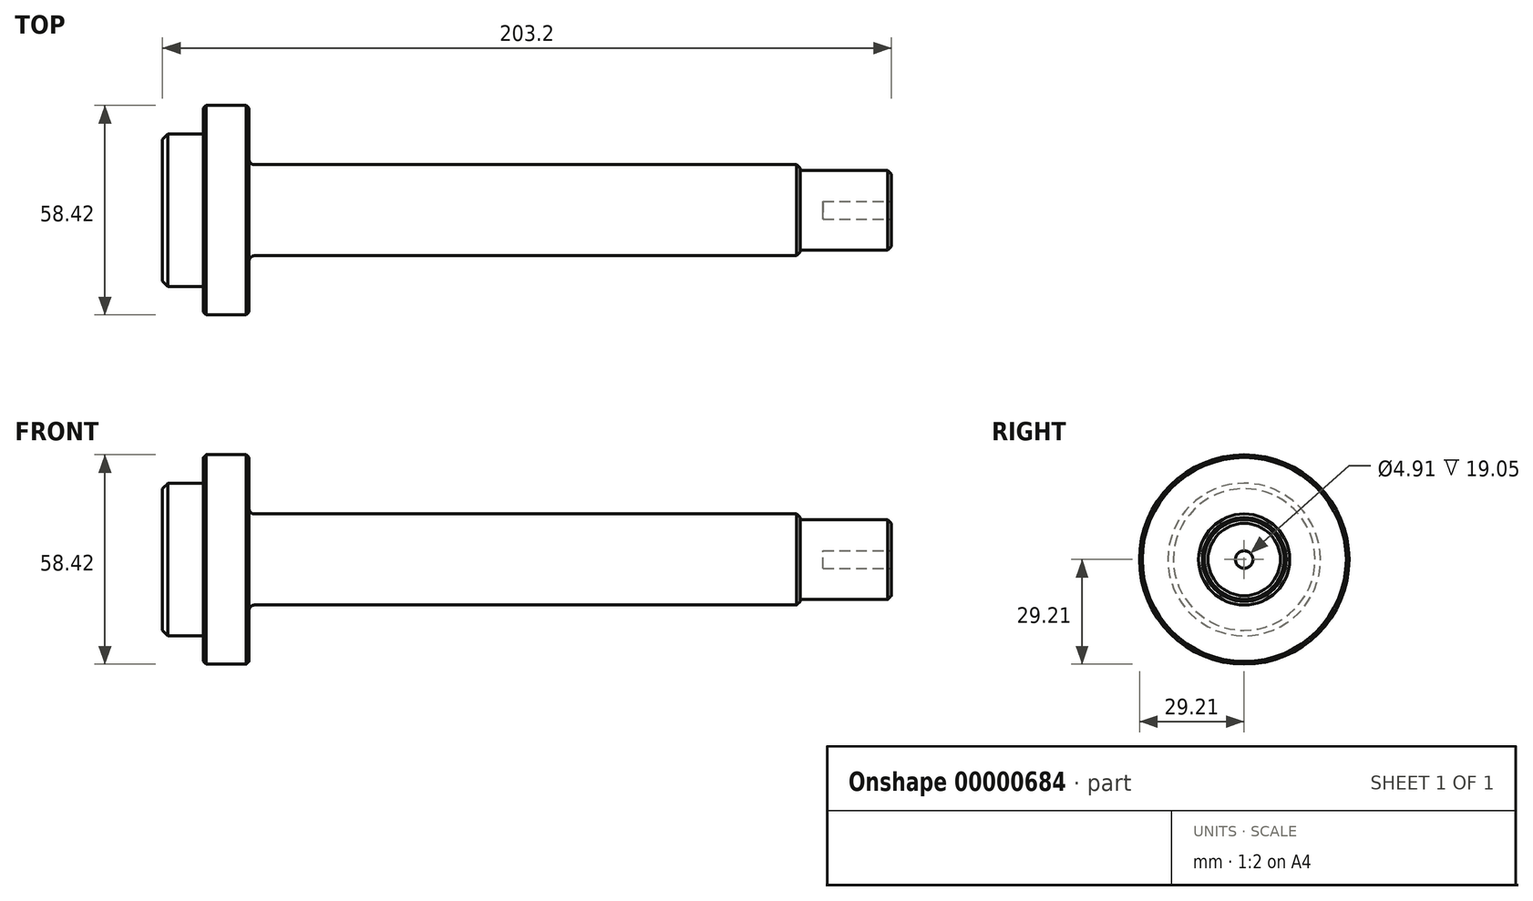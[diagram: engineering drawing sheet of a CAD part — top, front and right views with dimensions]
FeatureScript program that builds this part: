
annotation { "Feature Type Name" : "Feature", "Feature Type Description" : "" }
export const myFeature = defineFeature(function(context is Context, id is Id, definition is map)
    precondition{}
    {
        {
            var Q0;
            Q0=qCreatedBy(makeId("Front.planeOp"),FACE);
            var sketch = newSketch(context, id + "F0", { "sketchPlane" : qUnion([Q0])});
            skLineSegment(sketch, "E0", {"start": v(0, 0) * mm, "end": v(203.2, 0) * mm, "construction": true});
            skLineSegment(sketch, "E1", {"start": v(0, 0) * mm, "end": v(0, 21.27) * mm});
            skLineSegment(sketch, "E2", {"start": v(0, 21.27) * mm, "end": v(11.43, 21.27) * mm});
            skLineSegment(sketch, "E3", {"start": v(11.43, 21.27) * mm, "end": v(11.43, 29.2) * mm});
            skLineSegment(sketch, "E4", {"start": v(11.43, 29.2) * mm, "end": v(24.13, 29.2) * mm});
            skLineSegment(sketch, "E5", {"start": v(24.13, 29.2) * mm, "end": v(24.13, 14.22) * mm});
            skLineSegment(sketch, "E6", {"start": v(25.65, 12.7) * mm, "end": v(177.8, 12.7) * mm});
            skLineSegment(sketch, "E7", {"start": v(177.8, 12.7) * mm, "end": v(177.8, 11.11) * mm});
            skLineSegment(sketch, "E8", {"start": v(177.8, 11.11) * mm, "end": v(203.2, 11.11) * mm});
            skLineSegment(sketch, "E9", {"start": v(203.2, 11.11) * mm, "end": v(203.2, 0) * mm});
            skLineSegment(sketch, "E10", {"start": v(0, 0) * mm, "end": v(203.2, 0) * mm});
            skPoint(sketch, "E11.visualSharp", {"position": v(24.13, 12.7) * mm});
            skArc(sketch, "E11.filletArc", {"start": v(24.13, 14.22) * mm, "mid": v(24.58, 13.15) * mm, "end": v(25.65, 12.7) * mm});
            skSolve(sketch);
        }
        {
            var Q0;
            Q0=makeQuery(id+"F0.imprint","IMPRINT",FACE,{"disambiguationData":[TD([[makeQuery(id+"F0.imprint","IMPRINT",EDGE,{"derivedFrom":sQuery(id+"F0.wireOp",EDGE,"E1")}),-1.0]])]});
            var Q1;
            Q1=sQuery(id+"F0.wireOp",EDGE,"E10");
            revolve(context, id + "F1", {"entities" : qUnion([Q0]), "axis" : qUnion([Q1]), "revolveType" : RevolveType.FULL});
        }
        {
            var Q0;
            Q0=makeQuery(id+"F1.opRevolve","SWEPT_EDGE",EDGE,{"disambiguationData":[OSD([sQuery(id+"F0.wireOp",EDGE,"E3"),sQuery(id+"F0.wireOp",EDGE,"E4")])]});
            var Q1;
            Q1=makeQuery(id+"F1.opRevolve","SWEPT_EDGE",EDGE,{"disambiguationData":[OSD([sQuery(id+"F0.wireOp",EDGE,"E4"),sQuery(id+"F0.wireOp",EDGE,"E5")])]});
            chamfer(context, id + "F2", {"entities" : qUnion([Q0, Q1]), "chamferType" : ChamferType.OFFSET_ANGLE, "width" : 0.76 * mm, "oppositeDirection" : false, "angle" : 45 * degree, "tangentPropagation" : true});
        }
        {
            var Q0;
            Q0=makeQuery(id+"F1.opRevolve","SWEPT_EDGE",EDGE,{"disambiguationData":[OSD([sQuery(id+"F0.wireOp",EDGE,"E1"),sQuery(id+"F0.wireOp",EDGE,"E2")])]});
            chamfer(context, id + "F3", {"entities" : qUnion([Q0]), "chamferType" : ChamferType.OFFSET_ANGLE, "width" : 1.52 * mm, "oppositeDirection" : false, "angle" : 45 * degree, "tangentPropagation" : true});
        }
        {
            var Q0;
            Q0=makeQuery(id+"F1.opRevolve","SWEPT_EDGE",EDGE,{"disambiguationData":[OSD([sQuery(id+"F0.wireOp",EDGE,"E6"),sQuery(id+"F0.wireOp",EDGE,"E7")])]});
            var Q1;
            Q1=makeQuery(id+"F1.opRevolve","SWEPT_EDGE",EDGE,{"disambiguationData":[OSD([sQuery(id+"F0.wireOp",EDGE,"E8"),sQuery(id+"F0.wireOp",EDGE,"E9")])]});
            chamfer(context, id + "F4", {"entities" : qUnion([Q0, Q1]), "chamferType" : ChamferType.OFFSET_ANGLE, "width" : 1.02 * mm, "oppositeDirection" : false, "angle" : 45 * degree, "tangentPropagation" : true});
        }
        {
            var Q0;
            Q0=makeQuery(id+"F1.opRevolve","SWEPT_FACE",FACE,{"disambiguationData":[OSD([sQuery(id+"F0.wireOp",EDGE,"E9")])]});
            var sketch = newSketch(context, id + "F5", { "sketchPlane" : qUnion([Q0])});
            skCircle(sketch, "E12", {"center": v(0, 0) * mm, "radius": 2.46 * mm});
            skSolve(sketch);
        }
        {
            var Q0;
            Q0=makeQuery(id+"F5.imprint","IMPRINT",FACE,{"disambiguationData":[TD([[makeQuery(id+"F5.imprint","IMPRINT",EDGE,{"derivedFrom":sQuery(id+"F5.wireOp",EDGE,"E12")}),1.0]])]});
            extrude(context, id + "F6", {"entities" : qUnion([Q0]), "operationType" : NewBodyOperationType.REMOVE, "oppositeDirection" : true, "depth" : 19.05 * mm});
        }
    });
